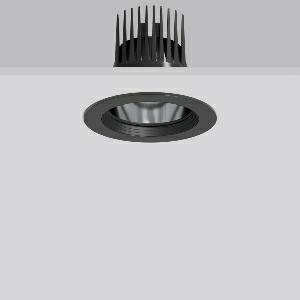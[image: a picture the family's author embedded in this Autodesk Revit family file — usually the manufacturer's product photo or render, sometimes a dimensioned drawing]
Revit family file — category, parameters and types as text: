
# Revit family: heledon_maxi_e_901759_003_1_4f1a
name_source: partatom
category: Lighting Fixtures
units: mm (PartAtom-declared; Revit-internal decimal feet)

## family parameters
Cut with Voids When Loaded = No
Host = Face
Light Source = No
Part Type = Normal
Room Calculation Point = No
Round Connector Dimension = Use Diameter
Shared = No

## types (1)
- HELEDON maxi E (1 x LED Modul 940, 3350 lm, 4000)
    Apparent Load = 25 VA
    Approval mark = CE
    CIE Flux Codes = 97 100 100 100 100
    Color Rendering = 92
    Color Temperature = 4000
    Default Elevation = 1800 mm
    Description = Series: HELEDON maxi
Round recessed downlight. Housing: die-cast aluminium, powder-coated. Black plastic ring and recessed LED to prevent glare from the side. Optical assembly with reflector made of MIRO-Silver with 98% total light reflection for outstanding efficiency - can be changed without tools. Best colour rendering index Ra>90. Suitable for Recessed ceiling mounting. Installation without tools thanks to spring fastening system. Including separate LED converter with connecting cable 600 mm.High quality converter without flickering and stroboscopic effect. Through-wiring box (5 pole) available as accessory. The following accessories can be mounted without use of tools: interchangeable lenses, decorative glasses, honeycomb louvre, clear and frosted diffusers, white interchangeable plastic ring. 
Colour: deep black, matt (RAL 9005)
Diameter: 162 mm
Height: 3 mm
Cut-out diameter: 152 mm
Recess height: 200 mm
Luminaire: recess height: 135 mm
Lamp: LED
Socket: without socket
Colour temperature: 4000K
Colour rendering index (CRI): 92
System power: 25 W
Rated luminous flux: 3350 lm
Luminous efficiency: 134 lm/W
Control gear: Regulated power supply
Protection class: II
Type of protection: IP 20
    Height = 0 mm  [stored 0 ft]
    Lamp = 1 x LED Modul 940
    Lamp Light Flux = 3350 lm
    Lamp count = 1
    Length = 162 mm
    Lifetime = 50000 h
    Luminous efficacy = 134 lm/W
    Manufacturer = RZB
    ModVariant = No
    Model = 901759.003.1
    Mounting Place = Ceiling
    Mounting Type = Recessed
    Number of Poles = 1
    OnlyDefault = Yes
    Power Factor = 1
    Product Name = HELEDON maxi E
    Product group = Recessed downlights
    ProductGroupID = 402
    Protection Class = Protection class II
    Protection Degree = IP 20
    RLX_Detail_Level = 1
    RLX_Emergency_Light_Flux = 0 lm
    RLX_Emergency_Type = 0
    RLX_Emergency_Type_DB = No
    RlxData = <blob elided: 121849 chars, md5=0f0466c1>
    Socket = socket
    Standby Power = 0 W
    System Light Flux = 3350 lm
    System Power = 25 W
    Type Comments = Product without accessories
    Type Image = 901662.003.jpg
    URL = http://relux.com
    VarID = ---
    Voltage = 230 V
    Voltage Range = 220-240 V
    Weight = 0.00 kg
    Width = 0 mm  [stored 0 ft]

note: [stored X ft] marks values corroborated as IEEE doubles in the binary element streams (Revit-internal decimal feet)

## geometry (parser evidence)
native form markers: Blend x4, Sweep x13
no freeform markers — native parametric forms only
